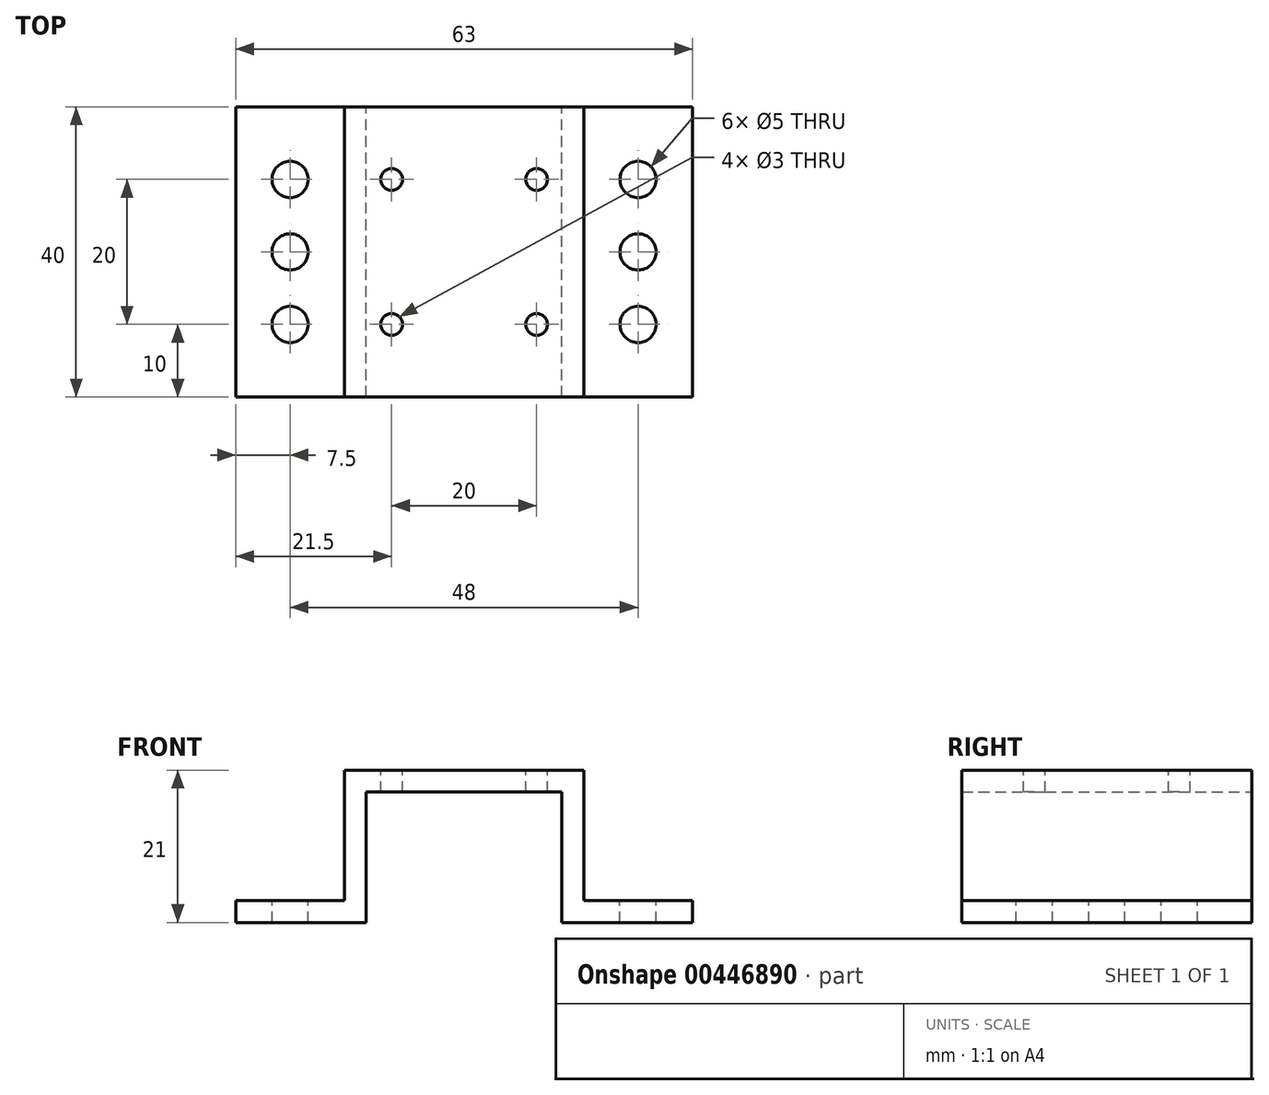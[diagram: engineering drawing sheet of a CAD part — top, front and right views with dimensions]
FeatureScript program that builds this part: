
annotation { "Feature Type Name" : "Feature", "Feature Type Description" : "" }
export const myFeature = defineFeature(function(context is Context, id is Id, definition is map)
    precondition{}
    {
        {
            var Q0;
            Q0=qCreatedBy(makeId("Front.planeOp"),FACE);
            var sketch = newSketch(context, id + "F0", { "sketchPlane" : qUnion([Q0])});
            skLineSegment(sketch, "E0", {"start": v(0, 0) * mm, "end": v(-13.5, 0) * mm});
            skLineSegment(sketch, "E1", {"start": v(-13.5, 0) * mm, "end": v(-13.5, -18) * mm});
            skLineSegment(sketch, "E2", {"start": v(-13.5, -18) * mm, "end": v(-31.5, -18) * mm});
            skLineSegment(sketch, "E3", {"start": v(-31.5, -18) * mm, "end": v(-31.5, -15) * mm});
            skLineSegment(sketch, "E4", {"start": v(-31.5, -15) * mm, "end": v(-16.5, -15) * mm});
            skLineSegment(sketch, "E5", {"start": v(-16.5, -15) * mm, "end": v(-16.5, 3) * mm});
            skLineSegment(sketch, "E6", {"start": v(-16.5, 3) * mm, "end": v(0, 3) * mm});
            skLineSegment(sketch, "E7", {"start": v(0, 3) * mm, "end": v(16.5, 3) * mm});
            skLineSegment(sketch, "E8", {"start": v(16.5, 3) * mm, "end": v(16.5, -15) * mm});
            skLineSegment(sketch, "E9", {"start": v(16.5, -15) * mm, "end": v(31.5, -15) * mm});
            skLineSegment(sketch, "E10", {"start": v(31.5, -15) * mm, "end": v(31.5, -18) * mm});
            skLineSegment(sketch, "E11", {"start": v(31.5, -18) * mm, "end": v(13.5, -18) * mm});
            skLineSegment(sketch, "E12", {"start": v(13.5, -18) * mm, "end": v(13.5, 0) * mm});
            skLineSegment(sketch, "E13", {"start": v(13.5, 0) * mm, "end": v(0, 0) * mm});
            skLineSegment(sketch, "E14", {"start": v(-20, -13.5) * mm, "end": v(-18, -13.5) * mm, "construction": true});
            skLineSegment(sketch, "E15", {"start": v(-18, -13.5) * mm, "end": v(-18, 4.5) * mm, "construction": true});
            skLineSegment(sketch, "E16", {"start": v(-18, 4.5) * mm, "end": v(18, 4.5) * mm, "construction": true});
            skLineSegment(sketch, "E17", {"start": v(18, 4.5) * mm, "end": v(18, -13.5) * mm, "construction": true});
            skLineSegment(sketch, "E18", {"start": v(18, -13.5) * mm, "end": v(20, -13.5) * mm, "construction": true});
            skLineSegment(sketch, "E19", {"start": v(20, -13.5) * mm, "end": v(20, 6.5) * mm, "construction": true});
            skLineSegment(sketch, "E20", {"start": v(20, 6.5) * mm, "end": v(-20, 6.5) * mm, "construction": true});
            skLineSegment(sketch, "E21", {"start": v(-20, 6.5) * mm, "end": v(-20, -13.5) * mm, "construction": true});
            skPoint(sketch, "E22", {"position": v(0, 6.5) * mm});
            skSolve(sketch);
        }
        {
            var Q0;
            Q0=makeQuery(id+"F0.imprint","IMPRINT",FACE,{"disambiguationData":[TD([[makeQuery(id+"F0.imprint","IMPRINT",EDGE,{"derivedFrom":sQuery(id+"F0.wireOp",EDGE,"E0")}),-1.0]])]});
            extrude(context, id + "F1", {"entities" : qUnion([Q0]), "depth" : 40 * mm});
        }
        {
            var Q0;
            Q0=makeQuery(id+"F1.opExtrude","SWEPT_FACE",FACE,{"disambiguationData":[OSD([sQuery(id+"F0.wireOp",EDGE,"E6"),sQuery(id+"F0.wireOp",EDGE,"E7")])]});
            var sketch = newSketch(context, id + "F2", { "sketchPlane" : qUnion([Q0])});
            skLineSegment(sketch, "E23.bottom", {"start": v(10, -30) * mm, "end": v(-10, -30) * mm, "construction": true});
            skLineSegment(sketch, "E23.top", {"start": v(10, -10) * mm, "end": v(-10, -10) * mm, "construction": true});
            skLineSegment(sketch, "E23.left", {"start": v(10, -30) * mm, "end": v(10, -10) * mm, "construction": true});
            skLineSegment(sketch, "E23.right", {"start": v(-10, -30) * mm, "end": v(-10, -10) * mm, "construction": true});
            skPoint(sketch, "E23.middle", {"position": v(0, -20) * mm});
            skPoint(sketch, "E23.middle.positionSnap0", {"position": v(0, 0) * mm});
            skPoint(sketch, "E23.middle.positionSnap1", {"position": v(-16.5, -20) * mm});
            skPoint(sketch, "E23.centerSnap0", {"position": v(0, 0) * mm});
            skPoint(sketch, "E23.centerSnap1", {"position": v(-16.5, -20) * mm});
            skCircle(sketch, "E24", {"center": v(-10, -10) * mm, "radius": 1.5 * mm});
            skCircle(sketch, "E25", {"center": v(10, -10) * mm, "radius": 1.5 * mm});
            skCircle(sketch, "E26", {"center": v(10, -30) * mm, "radius": 1.5 * mm});
            skCircle(sketch, "E27", {"center": v(-10, -30) * mm, "radius": 1.5 * mm});
            skSolve(sketch);
        }
        {
            var Q0;
            Q0=makeQuery(id+"F2.imprint","IMPRINT",FACE,{"disambiguationData":[TD([[makeQuery(id+"F2.imprint","IMPRINT",EDGE,{"derivedFrom":sQuery(id+"F2.wireOp",EDGE,"E24")}),1.0]])]});
            var Q1;
            Q1=makeQuery(id+"F2.imprint","IMPRINT",FACE,{"disambiguationData":[TD([[makeQuery(id+"F2.imprint","IMPRINT",EDGE,{"derivedFrom":sQuery(id+"F2.wireOp",EDGE,"E25")}),1.0]])]});
            var Q2;
            Q2=makeQuery(id+"F2.imprint","IMPRINT",FACE,{"disambiguationData":[TD([[makeQuery(id+"F2.imprint","IMPRINT",EDGE,{"derivedFrom":sQuery(id+"F2.wireOp",EDGE,"E26")}),1.0]])]});
            var Q3;
            Q3=makeQuery(id+"F2.imprint","IMPRINT",FACE,{"disambiguationData":[TD([[makeQuery(id+"F2.imprint","IMPRINT",EDGE,{"derivedFrom":sQuery(id+"F2.wireOp",EDGE,"E27")}),1.0]])]});
            extrude(context, id + "F3", {"entities" : qUnion([Q0, Q1, Q2, Q3]), "operationType" : NewBodyOperationType.REMOVE, "oppositeDirection" : true, "depth" : 25 * mm});
        }
        {
            var Q0;
            Q0=makeQuery(id+"F1.opExtrude","SWEPT_FACE",FACE,{"disambiguationData":[OSD([sQuery(id+"F0.wireOp",EDGE,"E4")])]});
            var sketch = newSketch(context, id + "F4", { "sketchPlane" : qUnion([Q0])});
            skLineSegment(sketch, "E28", {"start": v(-24, -40) * mm, "end": v(-24, -20) * mm, "construction": true});
            skPoint(sketch, "E28.endSnap0", {"position": v(-31.5, -20) * mm});
            skLineSegment(sketch, "E29", {"start": v(-24, 0) * mm, "end": v(-24, -20) * mm, "construction": true});
            skCircle(sketch, "E30", {"center": v(-24, -20) * mm, "radius": 2.5 * mm});
            skCircle(sketch, "E31", {"center": v(-24, -10) * mm, "radius": 2.5 * mm});
            skCircle(sketch, "E32", {"center": v(-24, -30) * mm, "radius": 2.5 * mm});
            skSolve(sketch);
        }
        {
            var Q0;
            Q0=makeQuery(id+"F4.imprint","IMPRINT",FACE,{"disambiguationData":[TD([[makeQuery(id+"F4.imprint","IMPRINT",EDGE,{"derivedFrom":sQuery(id+"F4.wireOp",EDGE,"E32")}),1.0]])]});
            var Q1;
            Q1=makeQuery(id+"F4.imprint","IMPRINT",FACE,{"disambiguationData":[TD([[makeQuery(id+"F4.imprint","IMPRINT",EDGE,{"derivedFrom":sQuery(id+"F4.wireOp",EDGE,"E30")}),1.0]])]});
            var Q2;
            Q2=makeQuery(id+"F4.imprint","IMPRINT",FACE,{"disambiguationData":[TD([[makeQuery(id+"F4.imprint","IMPRINT",EDGE,{"derivedFrom":sQuery(id+"F4.wireOp",EDGE,"E31")}),1.0]])]});
            extrude(context, id + "F5", {"entities" : qUnion([Q0, Q1, Q2]), "operationType" : NewBodyOperationType.REMOVE, "oppositeDirection" : true, "depth" : 25 * mm});
        }
        {
            var Q0;
            Q0=makeQuery(id+"F1.opExtrude","SWEPT_FACE",FACE,{"disambiguationData":[OSD([sQuery(id+"F0.wireOp",EDGE,"E9")])]});
            var sketch = newSketch(context, id + "F6", { "sketchPlane" : qUnion([Q0])});
            skLineSegment(sketch, "E33", {"start": v(24, -40) * mm, "end": v(24, -20) * mm, "construction": true});
            skPoint(sketch, "E33.endSnap0", {"position": v(31.5, -20) * mm});
            skLineSegment(sketch, "E34", {"start": v(24, 0) * mm, "end": v(24, -20) * mm, "construction": true});
            skCircle(sketch, "E35", {"center": v(24, -30) * mm, "radius": 2.5 * mm});
            skCircle(sketch, "E36", {"center": v(24, -20) * mm, "radius": 2.5 * mm});
            skCircle(sketch, "E37", {"center": v(24, -10) * mm, "radius": 2.5 * mm});
            skSolve(sketch);
        }
        {
            var Q0;
            Q0=makeQuery(id+"F6.imprint","IMPRINT",FACE,{"disambiguationData":[TD([[makeQuery(id+"F6.imprint","IMPRINT",EDGE,{"derivedFrom":sQuery(id+"F6.wireOp",EDGE,"E35")}),1.0]])]});
            var Q1;
            Q1=makeQuery(id+"F6.imprint","IMPRINT",FACE,{"disambiguationData":[TD([[makeQuery(id+"F6.imprint","IMPRINT",EDGE,{"derivedFrom":sQuery(id+"F6.wireOp",EDGE,"E36")}),1.0]])]});
            var Q2;
            Q2=makeQuery(id+"F6.imprint","IMPRINT",FACE,{"disambiguationData":[TD([[makeQuery(id+"F6.imprint","IMPRINT",EDGE,{"derivedFrom":sQuery(id+"F6.wireOp",EDGE,"E37")}),1.0]])]});
            extrude(context, id + "F7", {"entities" : qUnion([Q0, Q1, Q2]), "operationType" : NewBodyOperationType.REMOVE, "oppositeDirection" : true, "depth" : 25 * mm});
        }
    });
